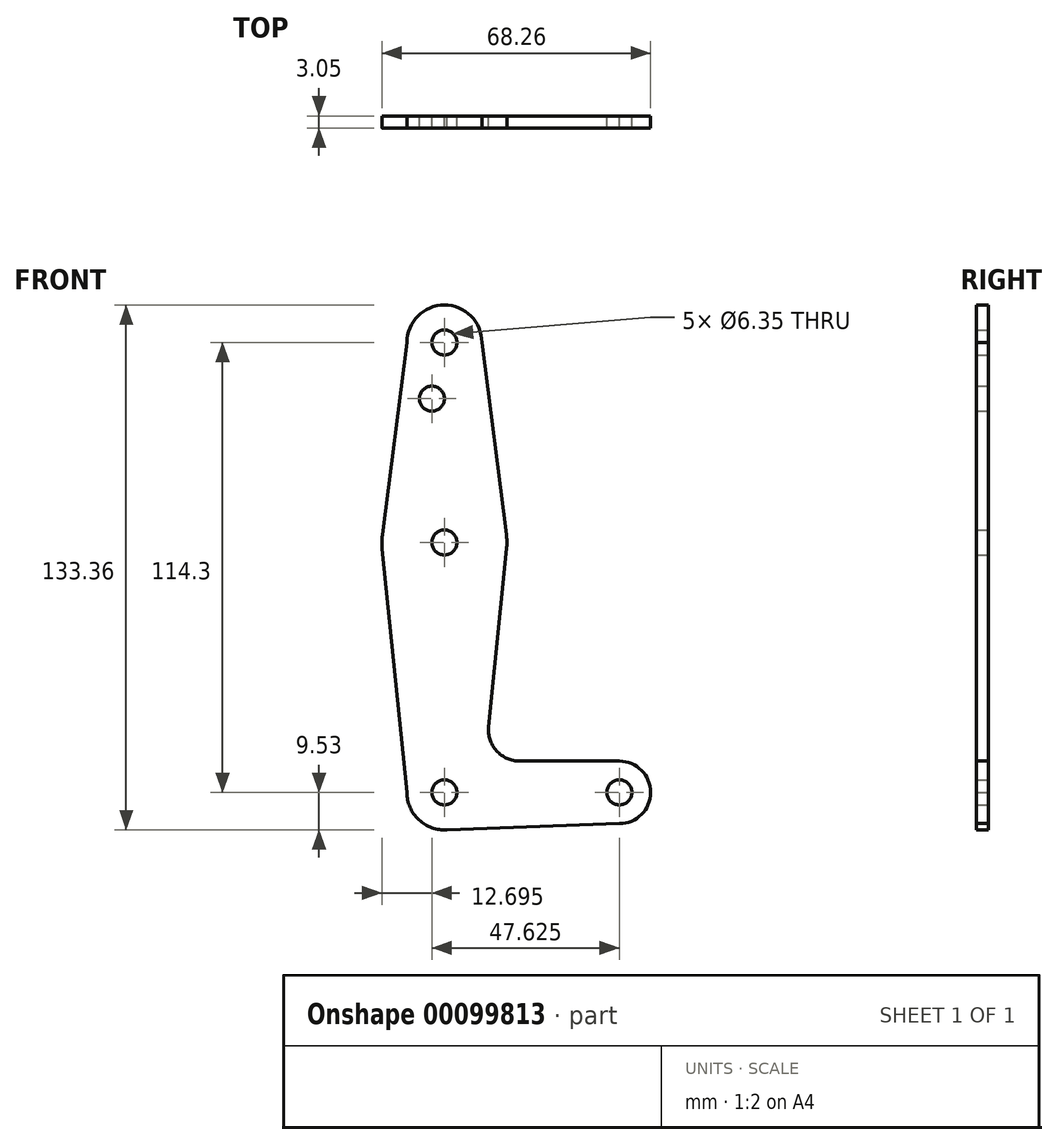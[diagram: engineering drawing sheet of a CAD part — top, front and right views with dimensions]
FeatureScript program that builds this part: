
annotation { "Feature Type Name" : "Feature", "Feature Type Description" : "" }
export const myFeature = defineFeature(function(context is Context, id is Id, definition is map)
    precondition{}
    {
        {
            var Q0;
            Q0=qCreatedBy(makeId("Front.planeOp"),FACE);
            var sketch = newSketch(context, id + "F0", { "sketchPlane" : qUnion([Q0])});
            skLineSegment(sketch, "E0", {"start": v(0, 0) * mm, "end": v(44.45, 0) * mm, "construction": true});
            skLineSegment(sketch, "E1", {"start": v(0, 0) * mm, "end": v(0, 114.3) * mm, "construction": true});
            skCircle(sketch, "E2", {"center": v(0, 114.3) * mm, "radius": 9.53 * mm});
            skCircle(sketch, "E3", {"center": v(0, 0) * mm, "radius": 9.53 * mm});
            skCircle(sketch, "E4", {"center": v(0, 63.5) * mm, "radius": 15.88 * mm});
            skCircle(sketch, "E5", {"center": v(44.45, 0) * mm, "radius": 7.94 * mm});
            skLineSegment(sketch, "E6", {"start": v(-9.53, 114.3) * mm, "end": v(-15.8, 65.13) * mm});
            skLineSegment(sketch, "E7", {"start": v(9.52, 114.3) * mm, "end": v(15.75, 65.5) * mm});
            skCircle(sketch, "E8", {"center": v(0, 114.3) * mm, "radius": 3.18 * mm});
            skCircle(sketch, "E9", {"center": v(0, 63.5) * mm, "radius": 3.18 * mm});
            skCircle(sketch, "E10", {"center": v(0, 0) * mm, "radius": 3.18 * mm});
            skCircle(sketch, "E11", {"center": v(44.45, 0) * mm, "radius": 3.18 * mm});
            skCircle(sketch, "E12", {"center": v(-3.18, 100.03) * mm, "radius": 3.18 * mm});
            skLineSegment(sketch, "E13", {"start": v(-15.8, 61.9) * mm, "end": v(-9.52, 0) * mm});
            skLineSegment(sketch, "E14", {"start": v(15.8, 61.91) * mm, "end": v(11.25, 16.68) * mm});
            skLineSegment(sketch, "E15", {"start": v(19.16, 7.94) * mm, "end": v(44.45, 7.94) * mm});
            skLineSegment(sketch, "E16", {"start": v(0, -9.52) * mm, "end": v(44.45, -7.94) * mm});
            skPoint(sketch, "E17.newPointA", {"position": v(9.57, 0) * mm});
            skArc(sketch, "E17.filletArc", {"start": v(11.25, 16.68) * mm, "mid": v(13.26, 10.55) * mm, "end": v(19.16, 7.94) * mm});
            skSolve(sketch);
        }
        {
            var Q0;
            Q0 = qSketchRegion(id + "F0", true);
            extrude(context, id + "F1", {"entities" : qUnion([Q0]), "depth" : 3.05 * mm});
        }
    });
